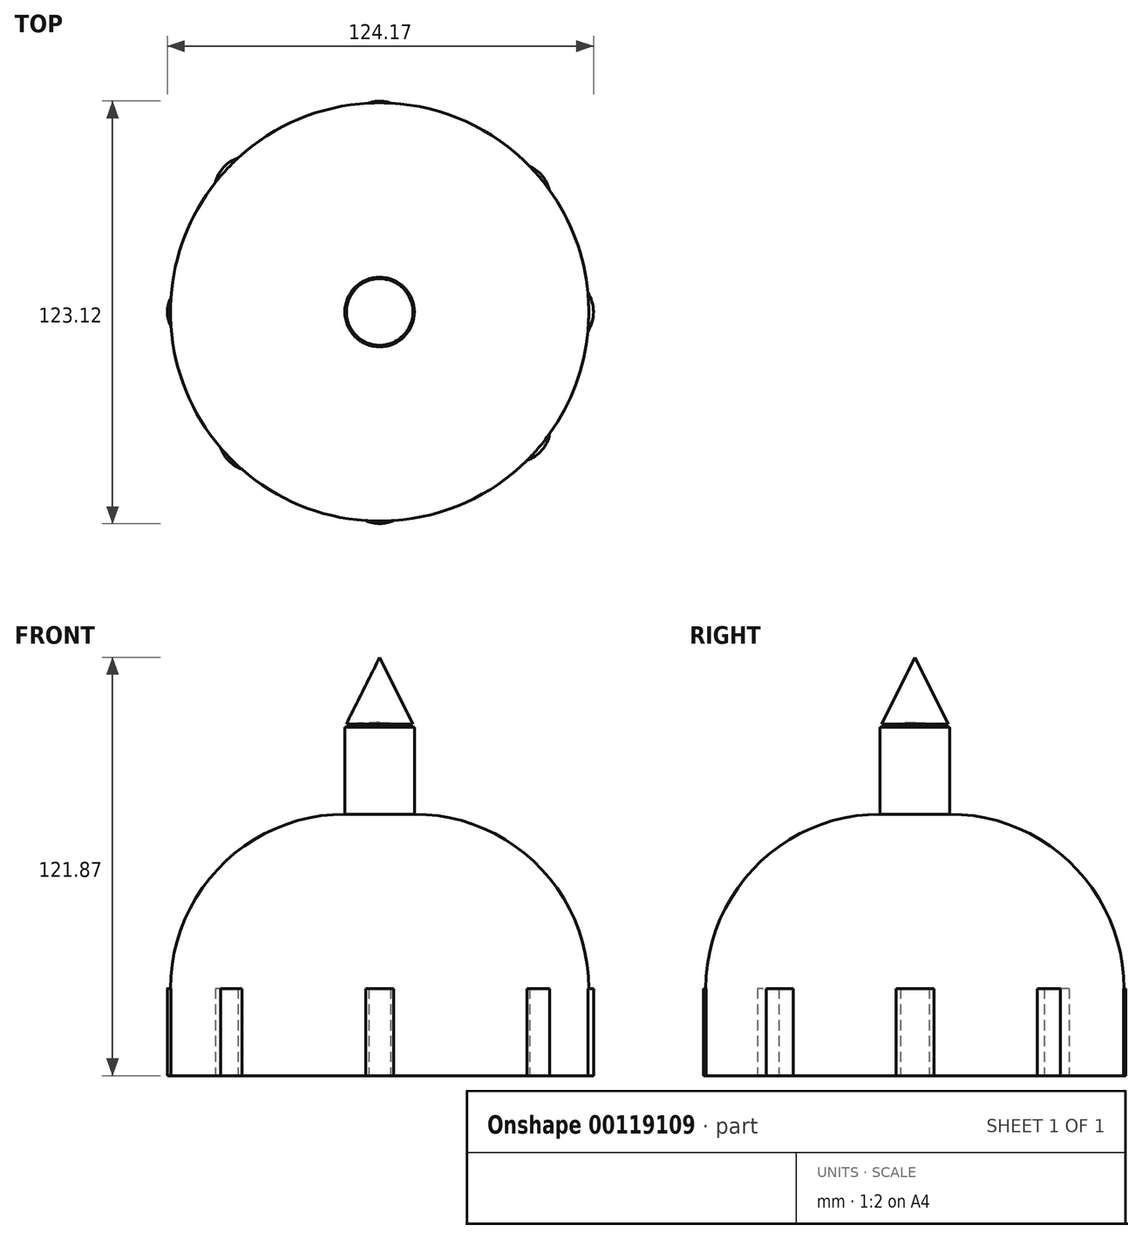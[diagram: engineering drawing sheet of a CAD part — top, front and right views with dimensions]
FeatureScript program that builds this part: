
annotation { "Feature Type Name" : "Feature", "Feature Type Description" : "" }
export const myFeature = defineFeature(function(context is Context, id is Id, definition is map)
    precondition{}
    {
        {
            var Q0;
            Q0=qCreatedBy(makeId("Top.planeOp"),FACE);
            var sketch = newSketch(context, id + "F0", { "sketchPlane" : qUnion([Q0])});
            skCircle(sketch, "E0", {"center": v(0, 0) * mm, "radius": 60.95 * mm});
            skSolve(sketch);
        }
        {
            var Q0;
            Q0=makeQuery(id+"F0.imprint","IMPRINT",FACE,{"disambiguationData":[TD([[makeQuery(id+"F0.imprint","IMPRINT",EDGE,{"derivedFrom":sQuery(id+"F0.wireOp",EDGE,"E0")}),1.0]])]});
            extrude(context, id + "F1", {"entities" : qUnion([Q0]), "depth" : 76.2 * mm});
        }
        {
            var Q0;
            Q0=makeQuery(id+"F1.opExtrude","CAP_EDGE",EDGE,{"disambiguationData":[OSD([sQuery(id+"F0.wireOp",EDGE,"E0")])],"isStart":false});
            fillet(context, id + "F2", {"entities" : qUnion([Q0]), "radius" : 50.8 * mm, "tangentPropagation" : true, "allowEdgeOverflow" : false});
        }
        {
            var Q0;
            Q0=makeQuery(id+"F1.opExtrude","CAP_FACE",FACE,{"disambiguationData":[OSD([sQuery(id+"F0.wireOp",EDGE,"E0")])],"isStart":false});
            extrude(context, id + "F3", {"entities" : qUnion([Q0]), "operationType" : NewBodyOperationType.ADD, "depth" : 25.4 * mm});
        }
        {
            var Q0;
            Q0=qCreatedBy(makeId("Front.planeOp"),FACE);
            var sketch = newSketch(context, id + "F4", { "sketchPlane" : qUnion([Q0])});
            skLineSegment(sketch, "E1", {"start": v(0, 102.94) * mm, "end": v(0, 121.87) * mm});
            skLineSegment(sketch, "E2", {"start": v(0, 121.87) * mm, "end": v(9.7, 102.48) * mm});
            skLineSegment(sketch, "E3", {"start": v(0, 102.94) * mm, "end": v(9.7, 102.48) * mm});
            skSolve(sketch);
        }
        {
            var Q0;
            Q0 = qSketchRegion(id + "F4", true);
            var Q1;
            Q1=sQuery(id+"F4.wireOp",EDGE,"E1");
            revolve(context, id + "F5", {"entities" : qUnion([Q0]), "axis" : qUnion([Q1]), "revolveType" : RevolveType.FULL});
        }
        {
            var Q0;
            Q0=qCreatedBy(makeId("Top.planeOp"),FACE);
            var sketch = newSketch(context, id + "F6", { "sketchPlane" : qUnion([Q0])});
            skCircle(sketch, "E4", {"center": v(0, -51.5) * mm, "radius": 10.16 * mm});
            skCircle(sketch, "E5", {"center": v(-52.95, 0) * mm, "radius": 8.9 * mm});
            skCircle(sketch, "E6", {"center": v(-36.7, -36.3) * mm, "radius": 10.16 * mm});
            skCircle(sketch, "E7", {"center": v(39.58, -33.68) * mm, "radius": 10.16 * mm});
            skCircle(sketch, "E8", {"center": v(52.17, 0) * mm, "radius": 10.16 * mm});
            skCircle(sketch, "E9", {"center": v(0, 52.56) * mm, "radius": 8.9 * mm});
            skCircle(sketch, "E10", {"center": v(39.58, 33.16) * mm, "radius": 10.16 * mm});
            skCircle(sketch, "E11", {"center": v(-38, 35.26) * mm, "radius": 10.16 * mm});
            skSolve(sketch);
        }
        {
            var Q0;
            Q0=makeQuery(id+"F6.imprint","IMPRINT",FACE,{"disambiguationData":[TD([[makeQuery(id+"F6.imprint","IMPRINT",EDGE,{"derivedFrom":sQuery(id+"F6.wireOp",EDGE,"E6")}),1.0]])]});
            var Q1;
            Q1=makeQuery(id+"F6.imprint","IMPRINT",FACE,{"disambiguationData":[TD([[makeQuery(id+"F6.imprint","IMPRINT",EDGE,{"derivedFrom":sQuery(id+"F6.wireOp",EDGE,"E4")}),1.0]])]});
            var Q2;
            Q2=makeQuery(id+"F6.imprint","IMPRINT",FACE,{"disambiguationData":[TD([[makeQuery(id+"F6.imprint","IMPRINT",EDGE,{"derivedFrom":sQuery(id+"F6.wireOp",EDGE,"E7")}),1.0]])]});
            var Q3;
            Q3=makeQuery(id+"F6.imprint","IMPRINT",FACE,{"disambiguationData":[TD([[makeQuery(id+"F6.imprint","IMPRINT",EDGE,{"derivedFrom":sQuery(id+"F6.wireOp",EDGE,"E8")}),1.0]])]});
            var Q4;
            Q4=makeQuery(id+"F6.imprint","IMPRINT",FACE,{"disambiguationData":[TD([[makeQuery(id+"F6.imprint","IMPRINT",EDGE,{"derivedFrom":sQuery(id+"F6.wireOp",EDGE,"E10")}),1.0]])]});
            var Q5;
            Q5=makeQuery(id+"F6.imprint","IMPRINT",FACE,{"disambiguationData":[TD([[makeQuery(id+"F6.imprint","IMPRINT",EDGE,{"derivedFrom":sQuery(id+"F6.wireOp",EDGE,"E9")}),1.0]])]});
            var Q6;
            Q6=makeQuery(id+"F6.imprint","IMPRINT",FACE,{"disambiguationData":[TD([[makeQuery(id+"F6.imprint","IMPRINT",EDGE,{"derivedFrom":sQuery(id+"F6.wireOp",EDGE,"E11")}),1.0]])]});
            var Q7;
            Q7=makeQuery(id+"F6.imprint","IMPRINT",FACE,{"disambiguationData":[TD([[makeQuery(id+"F6.imprint","IMPRINT",EDGE,{"derivedFrom":sQuery(id+"F6.wireOp",EDGE,"E5")}),1.0]])]});
            extrude(context, id + "F7", {"entities" : qUnion([Q0, Q1, Q2, Q3, Q4, Q5, Q6, Q7]), "operationType" : NewBodyOperationType.ADD, "depth" : 25.4 * mm});
        }
    });
